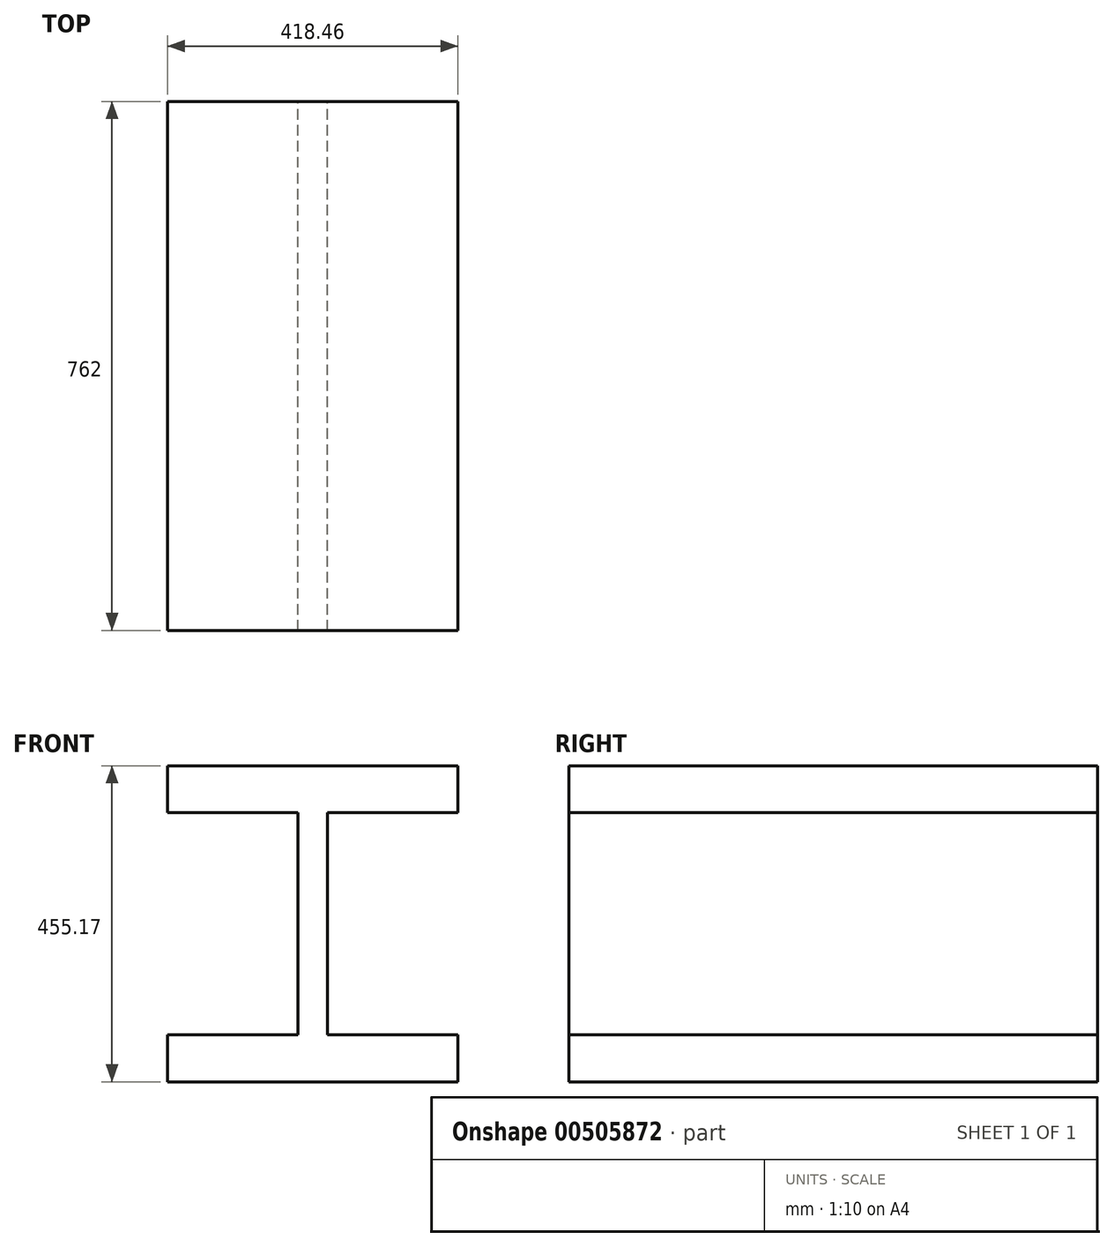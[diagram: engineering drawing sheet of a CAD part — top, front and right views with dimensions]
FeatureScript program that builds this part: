
annotation { "Feature Type Name" : "Feature", "Feature Type Description" : "" }
export const myFeature = defineFeature(function(context is Context, id is Id, definition is map)
    precondition{}
    {
        {
            var Q0;
            Q0=qCreatedBy(makeId("Front.planeOp"),FACE);
            var sketch = newSketch(context, id + "F0", { "sketchPlane" : qUnion([Q0])});
            skLineSegment(sketch, "E0", {"start": v(0, 0) * mm, "end": v(0, 95.05) * mm});
            skLineSegment(sketch, "E1", {"start": v(0, 95.05) * mm, "end": v(-188.21, 95.05) * mm});
            skLineSegment(sketch, "E2", {"start": v(-188.21, 95.05) * mm, "end": v(-188.21, 162.6) * mm});
            skLineSegment(sketch, "E3", {"start": v(-188.21, 162.6) * mm, "end": v(230.25, 162.6) * mm});
            skLineSegment(sketch, "E4", {"start": v(230.25, 162.6) * mm, "end": v(230.25, 95.05) * mm});
            skLineSegment(sketch, "E5", {"start": v(230.25, 95.05) * mm, "end": v(42.04, 95.05) * mm});
            skLineSegment(sketch, "E6", {"start": v(42.04, 95.05) * mm, "end": v(42.04, -225) * mm});
            skLineSegment(sketch, "E7", {"start": v(42.04, -225) * mm, "end": v(230.25, -225) * mm});
            skLineSegment(sketch, "E8", {"start": v(230.25, -225) * mm, "end": v(230.25, -292.56) * mm});
            skLineSegment(sketch, "E9", {"start": v(230.25, -292.56) * mm, "end": v(-188.21, -292.56) * mm});
            skLineSegment(sketch, "E10", {"start": v(-188.21, -292.56) * mm, "end": v(-188.21, -225) * mm});
            skLineSegment(sketch, "E11", {"start": v(-188.21, -225) * mm, "end": v(0, -225) * mm});
            skLineSegment(sketch, "E12", {"start": v(0, -225) * mm, "end": v(0, 0) * mm});
            skSolve(sketch);
        }
        {
            var Q0;
            Q0 = qSketchRegion(id + "F0", true);
            extrude(context, id + "F1", {"entities" : qUnion([Q0]), "depth" : 762 * mm});
        }
    });
